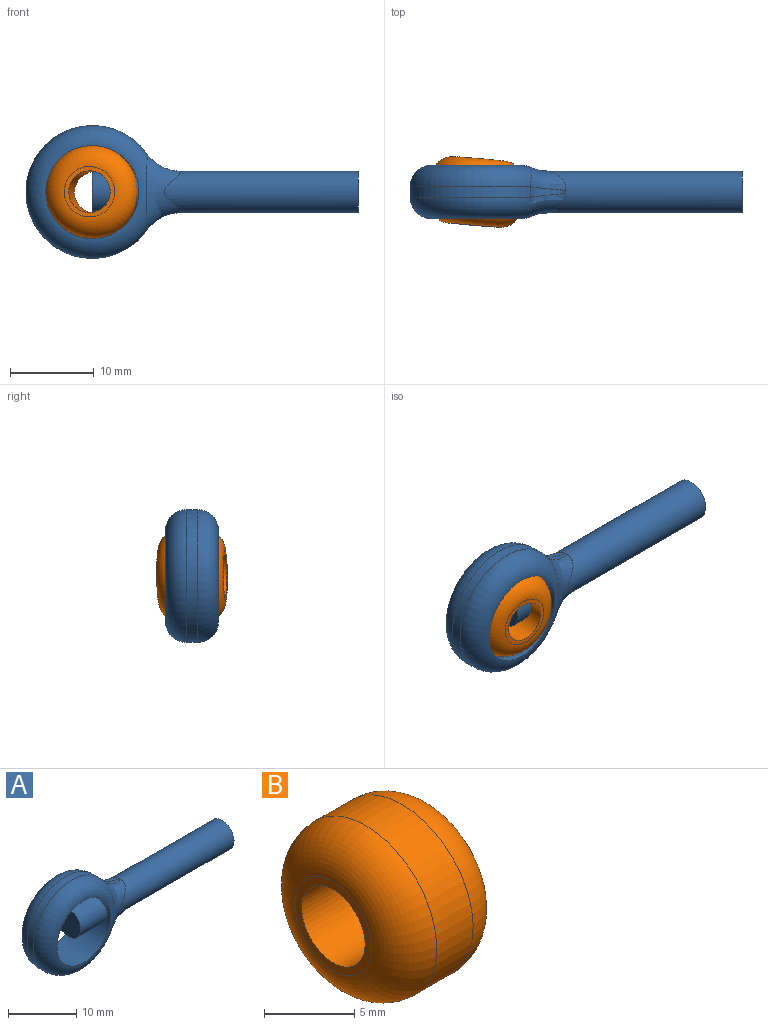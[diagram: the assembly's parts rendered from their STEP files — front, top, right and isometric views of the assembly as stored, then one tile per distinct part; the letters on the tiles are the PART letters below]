
ASSEMBLY  parts=2 mates=1
PART A: 12 faces, bbox 40.3x6.4x17.2 mm
  f0: cylinder r=5.56mm len=11.11mm, axis (0,1,0), area 201.8mm2, adj f4,f6,f7
  f1: cylinder r=7.94mm len=15.88mm, axis (0,1,0), area 51.3mm2, adj f6,f7,f9,f10
  f2: plane 4.98x4.98mm, normal (1,0,0), area 19.5mm2, adj f3
  f3: cylinder r=2.49mm len=23.18mm, axis (-1,0,0), area 342.6mm2, adj f2,f8,f9,f10,f11
  f4: cylinder r=2.49mm len=5.56mm, axis (-1,0,0), area 82.4mm2, adj f0,f5
  f5: plane 4.98x4.98mm, normal (-1,0,0), area 19.5mm2, adj f4
  f6: torus R=5.4mm, axis (0,1,0), area 149.5mm2, adj f0,f1,f8
  f7: torus R=5.4mm, axis (0,-1,0), area 149.5mm2, adj f0,f1,f11
  f8: bspline ~9.25x4.24mm, area 31.1mm2, adj f3,f6,f9,f10
  f9: bspline ~4.42x4.35mm, area 3.9mm2, adj f1,f3,f8,f11
  f10: bspline ~4.42x4.35mm, area 3.9mm2, adj f1,f3,f8,f11
  f11: bspline ~9.25x4.24mm, area 31.1mm2, adj f3,f7,f9,f10
PART B: 6 faces, bbox 7.9x12x12 mm
  f0: cylinder r=2.49mm len=7.94mm, axis (-1,0,0), area 124.1mm2, adj f2,f3
  f1: cylinder r=5.56mm len=11.11mm, axis (-1,0,0), area 99.8mm2, adj f4,f5
  f2: plane 6.03x6.03mm, normal (1,0,0), area 9.1mm2, adj f0,f5
  f3: plane 6.03x6.03mm, normal (-1,0,0), area 9.1mm2, adj f0,f4
  f4: torus R=3.02mm, axis (1,0,0), area 116.2mm2, adj f1,f3
  f5: torus R=3.02mm, axis (1,0,0), area 116.2mm2, adj f1,f2
PLACE A t=(-4.18,2.73,-1.45)mm fixed
PLACE B rot(axis=(0.47,-0.52,-0.72),112.9deg) t=(-3.84,3.51,-1.49)mm
MATE ball B.f1 <-> A.f1  axis (0.09,1,-0.01) through (-4.18,-0.44,-1.45)mm
